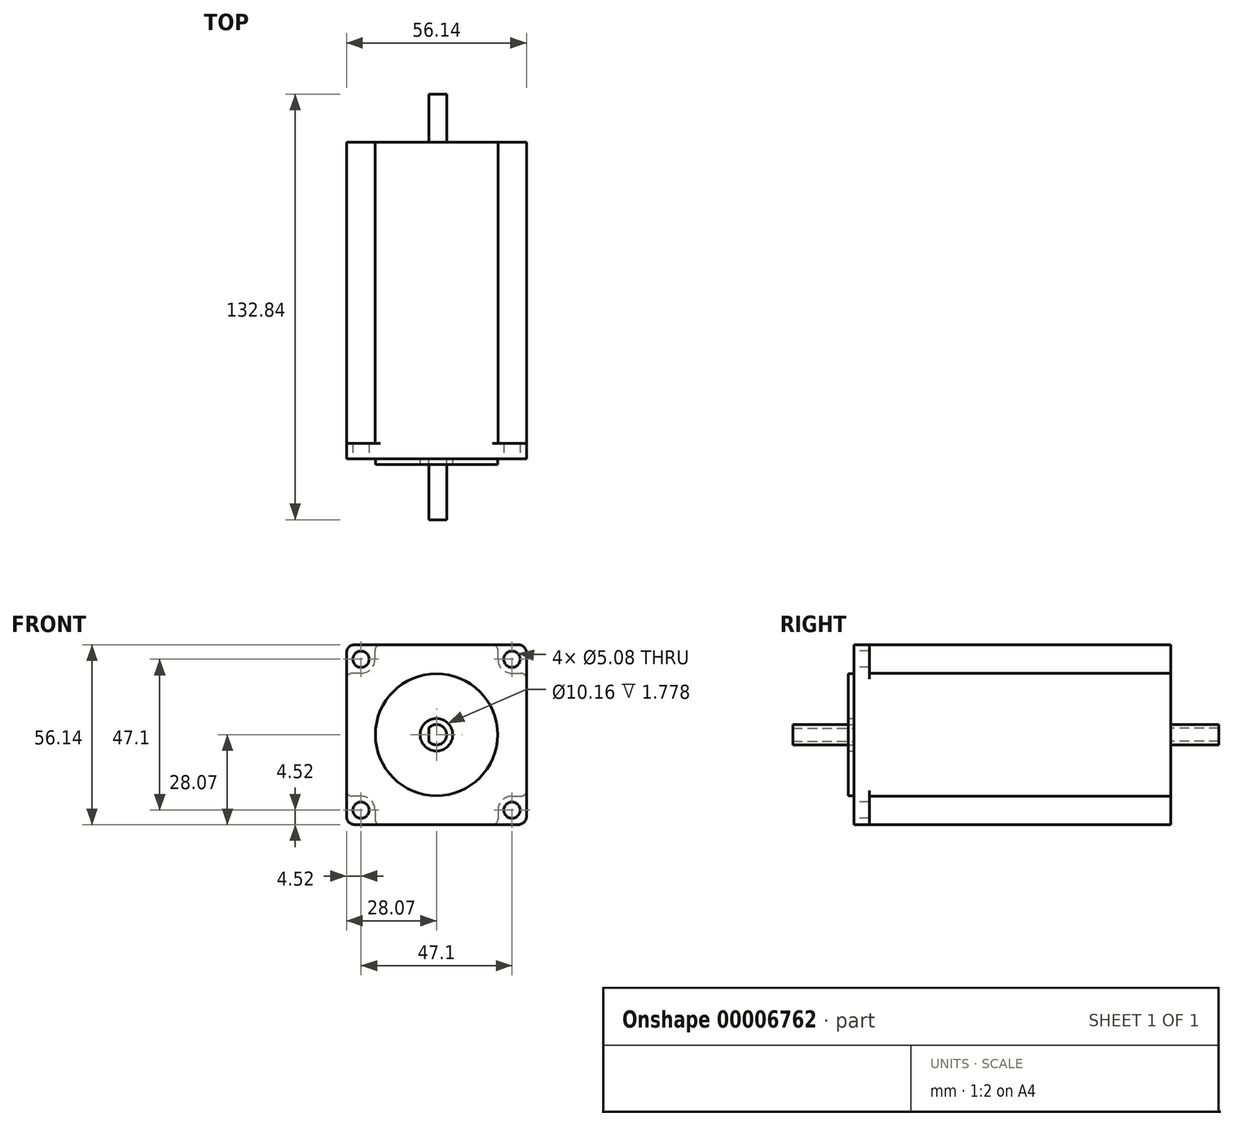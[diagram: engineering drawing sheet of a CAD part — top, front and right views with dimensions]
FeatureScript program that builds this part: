
annotation { "Feature Type Name" : "Feature", "Feature Type Description" : "" }
export const myFeature = defineFeature(function(context is Context, id is Id, definition is map)
    precondition{}
    {
        {
            var Q0;
            Q0=qCreatedBy(makeId("Front.planeOp"),FACE);
            var sketch = newSketch(context, id + "F0", { "sketchPlane" : qUnion([Q0])});
            skLineSegment(sketch, "E0.rect.bottom", {"start": v(25.53, -28.07) * mm, "end": v(-25.53, -28.07) * mm});
            skLineSegment(sketch, "E0.rect.top", {"start": v(25.53, 28.07) * mm, "end": v(-25.53, 28.07) * mm});
            skLineSegment(sketch, "E0.rect.left", {"start": v(28.07, -25.53) * mm, "end": v(28.07, 25.53) * mm});
            skLineSegment(sketch, "E0.rect.right", {"start": v(-28.07, -25.53) * mm, "end": v(-28.07, 25.53) * mm});
            skPoint(sketch, "E0.rect.middle", {"position": v(0, 0) * mm});
            skPoint(sketch, "E1.visualSharp", {"position": v(-28.07, 28.07) * mm});
            skArc(sketch, "E1.filletArc", {"start": v(-25.53, 28.07) * mm, "mid": v(-27.32, 27.32) * mm, "end": v(-28.07, 25.53) * mm});
            skPoint(sketch, "E2.visualSharp", {"position": v(28.07, 28.07) * mm});
            skArc(sketch, "E2.filletArc", {"start": v(28.07, 25.53) * mm, "mid": v(27.32, 27.32) * mm, "end": v(25.53, 28.07) * mm});
            skPoint(sketch, "E3.visualSharp", {"position": v(28.07, -28.07) * mm});
            skArc(sketch, "E3.filletArc", {"start": v(25.53, -28.07) * mm, "mid": v(27.32, -27.32) * mm, "end": v(28.07, -25.53) * mm});
            skPoint(sketch, "E4.visualSharp", {"position": v(-28.07, -28.07) * mm});
            skArc(sketch, "E4.filletArc", {"start": v(-28.07, -25.53) * mm, "mid": v(-27.32, -27.32) * mm, "end": v(-25.53, -28.07) * mm});
            skCircle(sketch, "E5", {"center": v(-23.55, 23.55) * mm, "radius": 2.54 * mm});
            skCircle(sketch, "E6", {"center": v(23.55, 23.55) * mm, "radius": 2.54 * mm});
            skCircle(sketch, "E7", {"center": v(23.55, -23.55) * mm, "radius": 2.54 * mm});
            skCircle(sketch, "E8", {"center": v(-23.55, -23.55) * mm, "radius": 2.54 * mm});
            skLineSegment(sketch, "E9", {"start": v(-23.55, 23.55) * mm, "end": v(23.55, 23.55) * mm, "construction": true});
            skLineSegment(sketch, "E10", {"start": v(23.55, 23.55) * mm, "end": v(23.55, -23.55) * mm, "construction": true});
            skPoint(sketch, "E11", {"position": v(0, 23.55) * mm});
            skPoint(sketch, "E12", {"position": v(23.55, 0) * mm});
            skCircle(sketch, "E13", {"center": v(0, 0) * mm, "radius": 19.05 * mm});
            skCircle(sketch, "E14", {"center": v(0, 0) * mm, "radius": 5.08 * mm});
            skArc(sketch, "E15", {"start": v(-2.41, -2.06) * mm, "mid": v(3.18, 0) * mm, "end": v(-2.41, 2.06) * mm});
            skLineSegment(sketch, "E16", {"start": v(-2.41, 2.06) * mm, "end": v(-2.41, -2.06) * mm});
            skLineSegment(sketch, "E17", {"start": v(0, 0) * mm, "end": v(0, 37.58) * mm, "construction": true});
            skLineSegment(sketch, "E18", {"start": v(0, 0) * mm, "end": v(-50.04, 0) * mm, "construction": true});
            skArc(sketch, "E19", {"start": v(-23.55, 19.18) * mm, "mid": v(-20.46, 20.46) * mm, "end": v(-19.18, 23.55) * mm});
            skArc(sketch, "E20", {"start": v(-26.33, 19.18) * mm, "mid": v(-27.56, 18.67) * mm, "end": v(-28.07, 17.44) * mm});
            skArc(sketch, "E21", {"start": v(-17.44, 28.07) * mm, "mid": v(-18.67, 27.56) * mm, "end": v(-19.18, 26.33) * mm});
            skLineSegment(sketch, "E22", {"start": v(-23.55, 19.18) * mm, "end": v(-26.33, 19.18) * mm});
            skLineSegment(sketch, "E23", {"start": v(-19.18, 23.55) * mm, "end": v(-19.18, 26.33) * mm});
            skArc(sketch, "E24.MirrorCS", {"start": v(26.33, 19.18) * mm, "mid": v(27.56, 18.67) * mm, "end": v(28.07, 17.44) * mm});
            skLineSegment(sketch, "E25.MirrorCS", {"start": v(19.18, 23.55) * mm, "end": v(19.18, 26.33) * mm});
            skLineSegment(sketch, "E26.MirrorCS", {"start": v(23.55, 19.18) * mm, "end": v(26.33, 19.18) * mm});
            skArc(sketch, "E27.MirrorCS", {"start": v(23.55, 19.18) * mm, "mid": v(20.46, 20.46) * mm, "end": v(19.18, 23.55) * mm});
            skArc(sketch, "E28.MirrorCS", {"start": v(17.44, 28.07) * mm, "mid": v(18.67, 27.56) * mm, "end": v(19.18, 26.33) * mm});
            skArc(sketch, "E29.MirrorCS", {"start": v(26.33, -19.18) * mm, "mid": v(27.56, -18.67) * mm, "end": v(28.07, -17.44) * mm});
            skLineSegment(sketch, "E30.MirrorCS", {"start": v(23.55, -19.18) * mm, "end": v(26.33, -19.18) * mm});
            skArc(sketch, "E31.MirrorCS", {"start": v(23.55, -19.18) * mm, "mid": v(20.46, -20.46) * mm, "end": v(19.18, -23.55) * mm});
            skArc(sketch, "E32.MirrorCS", {"start": v(17.44, -28.07) * mm, "mid": v(18.67, -27.56) * mm, "end": v(19.18, -26.33) * mm});
            skLineSegment(sketch, "E33.MirrorCS", {"start": v(19.18, -23.55) * mm, "end": v(19.18, -26.33) * mm});
            skArc(sketch, "E34.MirrorCS", {"start": v(-26.33, -19.18) * mm, "mid": v(-27.56, -18.67) * mm, "end": v(-28.07, -17.44) * mm});
            skLineSegment(sketch, "E35.MirrorCS", {"start": v(-19.18, -23.55) * mm, "end": v(-19.18, -26.33) * mm});
            skLineSegment(sketch, "E36.MirrorCS", {"start": v(-23.55, -19.18) * mm, "end": v(-26.33, -19.18) * mm});
            skArc(sketch, "E37.MirrorCS", {"start": v(-23.55, -19.18) * mm, "mid": v(-20.46, -20.46) * mm, "end": v(-19.18, -23.55) * mm});
            skArc(sketch, "E38.MirrorCS", {"start": v(-17.44, -28.07) * mm, "mid": v(-18.67, -27.56) * mm, "end": v(-19.18, -26.33) * mm});
            skSolve(sketch);
        }
        {
            var Q0;
            Q0=makeQuery(id+"F0.imprint","IMPRINT",FACE,{"disambiguationData":[TD([[makeQuery(id+"F0.imprint","IMPRINT",EDGE,{"derivedFrom":sQuery(id+"F0.wireOp",EDGE,"E13")}),-1.0]])]});
            var Q1;
            Q1=makeQuery(id+"F0.imprint","IMPRINT",FACE,{"disambiguationData":[TD([[makeQuery(id+"F0.imprint","IMPRINT",EDGE,{"derivedFrom":sQuery(id+"F0.wireOp",EDGE,"E13")}),1.0]])]});
            var Q2;
            Q2=makeQuery(id+"F0.imprint","IMPRINT",FACE,{"disambiguationData":[TD([[makeQuery(id+"F0.imprint","IMPRINT",EDGE,{"derivedFrom":sQuery(id+"F0.wireOp",EDGE,"E15")}),1.0]])]});
            var Q3;
            Q3=makeQuery(id+"F0.imprint","IMPRINT",FACE,{"disambiguationData":[TD([[makeQuery(id+"F0.imprint","IMPRINT",EDGE,{"derivedFrom":sQuery(id+"F0.wireOp",EDGE,"E14")}),1.0]])]});
            extrude(context, id + "F1", {"entities" : qUnion([Q0, Q1, Q2, Q3]), "oppositeDirection" : true, "depth" : 98.8 * mm});
        }
        {
            var Q0;
            {var subQ3=sQuery(id+"F0.wireOp",EDGE,"E1.filletArc");Q0=makeQuery(id+"F0.imprint","IMPRINT",FACE,{"disambiguationData":[TD([[makeQuery(id+"F0.imprint","IMPRINT",EDGE,{"derivedFrom":subQ3}),1.0]])]});}
            var Q1;
            {var subQ3=sQuery(id+"F0.wireOp",EDGE,"E2.filletArc");Q1=makeQuery(id+"F0.imprint","IMPRINT",FACE,{"disambiguationData":[TD([[makeQuery(id+"F0.imprint","IMPRINT",EDGE,{"derivedFrom":subQ3}),1.0]])]});}
            var Q2;
            {var subQ3=sQuery(id+"F0.wireOp",EDGE,"E3.filletArc");Q2=makeQuery(id+"F0.imprint","IMPRINT",FACE,{"disambiguationData":[TD([[makeQuery(id+"F0.imprint","IMPRINT",EDGE,{"derivedFrom":subQ3}),1.0]])]});}
            var Q3;
            {var subQ3=sQuery(id+"F0.wireOp",EDGE,"E4.filletArc");Q3=makeQuery(id+"F0.imprint","IMPRINT",FACE,{"disambiguationData":[TD([[makeQuery(id+"F0.imprint","IMPRINT",EDGE,{"derivedFrom":subQ3}),1.0]])]});}
            extrude(context, id + "F2", {"entities" : qUnion([Q0, Q1, Q2, Q3]), "operationType" : NewBodyOperationType.ADD, "oppositeDirection" : true, "depth" : 4.83 * mm});
        }
        {
            var Q0;
            Q0=makeQuery(id+"F0.imprint","IMPRINT",FACE,{"disambiguationData":[TD([[makeQuery(id+"F0.imprint","IMPRINT",EDGE,{"derivedFrom":sQuery(id+"F0.wireOp",EDGE,"E13")}),1.0]])]});
            extrude(context, id + "F3", {"entities" : qUnion([Q0]), "operationType" : NewBodyOperationType.ADD, "depth" : 1.78 * mm});
        }
        {
            var Q0;
            Q0=makeQuery(id+"F0.imprint","IMPRINT",FACE,{"disambiguationData":[TD([[makeQuery(id+"F0.imprint","IMPRINT",EDGE,{"derivedFrom":sQuery(id+"F0.wireOp",EDGE,"E15")}),1.0]])]});
            extrude(context, id + "F4", {"entities" : qUnion([Q0]), "operationType" : NewBodyOperationType.ADD, "oppositeDirection" : true, "depth" : 113.8 * mm});
        }
        {
            var Q0;
            Q0=makeQuery(id+"F0.imprint","IMPRINT",FACE,{"disambiguationData":[TD([[makeQuery(id+"F0.imprint","IMPRINT",EDGE,{"derivedFrom":sQuery(id+"F0.wireOp",EDGE,"E15")}),1.0]])]});
            extrude(context, id + "F5", {"entities" : qUnion([Q0]), "operationType" : NewBodyOperationType.ADD, "depth" : 19.05 * mm});
        }
    });
